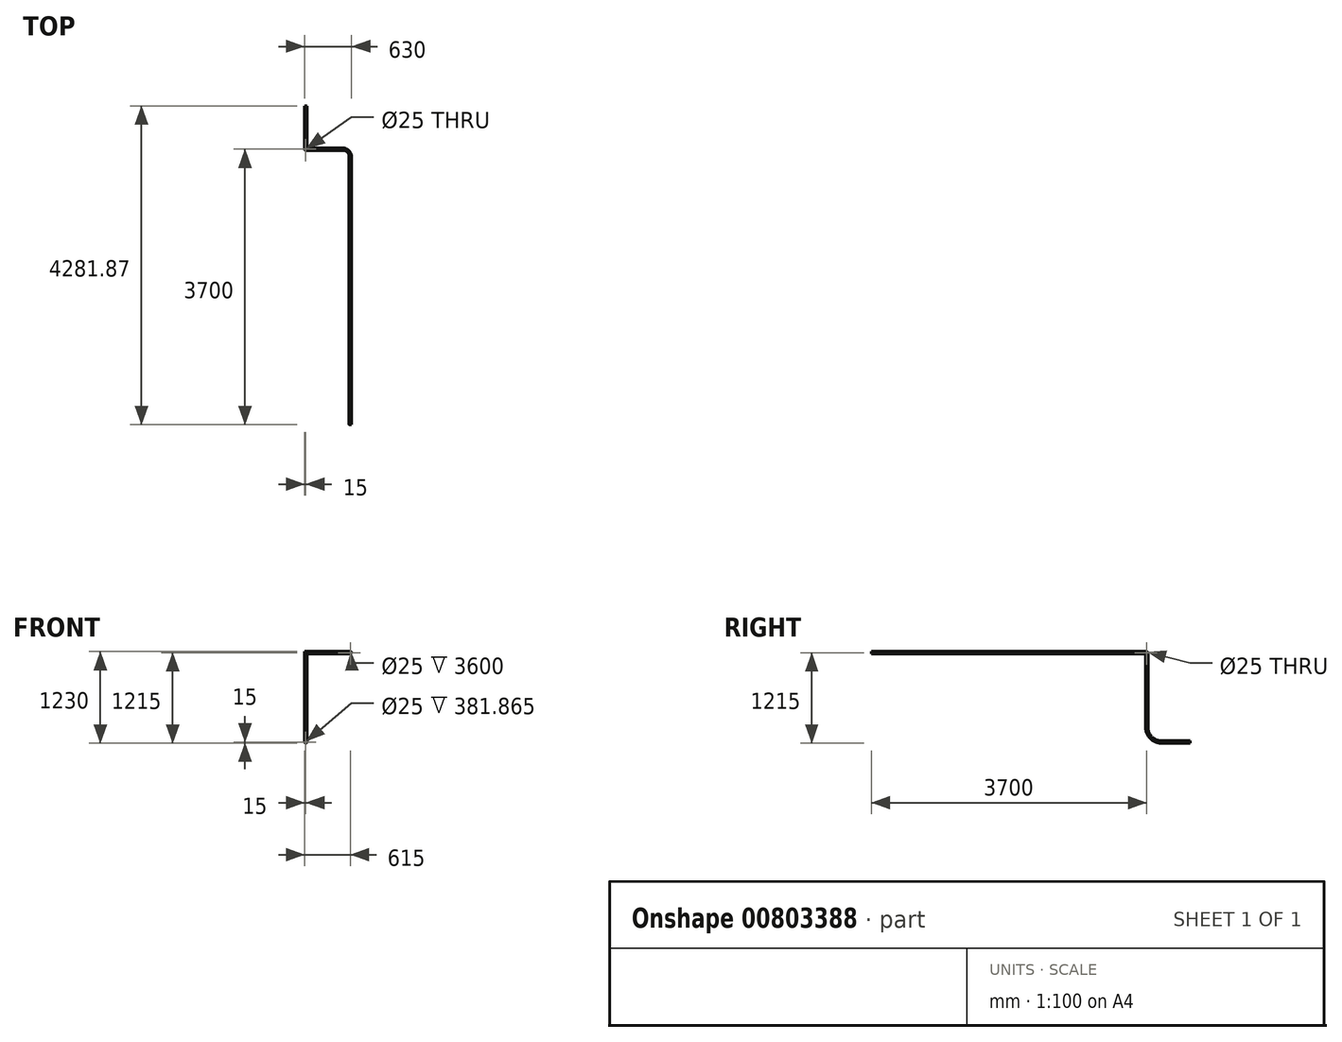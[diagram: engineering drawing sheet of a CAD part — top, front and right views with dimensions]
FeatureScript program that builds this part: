
annotation { "Feature Type Name" : "Feature", "Feature Type Description" : "" }
export const myFeature = defineFeature(function(context is Context, id is Id, definition is map)
    precondition{}
    {
        {
            var Q0;
            Q0=qCreatedBy(makeId("Front.planeOp"),FACE);
            var sketch = newSketch(context, id + "F0", { "sketchPlane" : qUnion([Q0])});
            skCircle(sketch, "E0", {"center": v(0, 0) * mm, "radius": 15 * mm});
            skCircle(sketch, "E1", {"center": v(0, 0) * mm, "radius": 12.5 * mm});
            skSolve(sketch);
        }
        {
            var Q0;
            Q0=qCreatedBy(makeId("Top.planeOp"),FACE);
            var sketch = newSketch(context, id + "F1", { "sketchPlane" : qUnion([Q0])});
            skLineSegment(sketch, "E2", {"start": v(0, 0) * mm, "end": v(0, 3600) * mm});
            skLineSegment(sketch, "E3", {"start": v(-100, 3700) * mm, "end": v(-600, 3700) * mm});
            skPoint(sketch, "E4.visualSharp", {"position": v(0, 3700) * mm});
            skArc(sketch, "E4.filletArc", {"start": v(0, 3600) * mm, "mid": v(-29.29, 3670.71) * mm, "end": v(-100, 3700) * mm});
            skSolve(sketch);
        }
        {
            var Q0;
            Q0=qCreatedBy(makeId("Right.planeOp"),FACE);
            cPlane(context, id + "F2", {"entities" : qUnion([Q0]), "cplaneType" : CPlaneType.OFFSET, "offset" : 600 * mm, "oppositeDirection" : true, "width" : 150 * mm, "height" : 150 * mm});
        }
        {
            var Q0;
            Q0=qCreatedBy(id+"F2.planeOp",FACE);
            var sketch = newSketch(context, id + "F3", { "sketchPlane" : qUnion([Q0])});
            skPoint(sketch, "E5.0", {"position": v(3700, 0) * mm});
            skLineSegment(sketch, "E6", {"start": v(3700, 0) * mm, "end": v(3700, -1000) * mm});
            skLineSegment(sketch, "E7", {"start": v(3900, -1200) * mm, "end": v(4281.87, -1200) * mm});
            skPoint(sketch, "E8.visualSharp", {"position": v(3700, -1200) * mm});
            skArc(sketch, "E8.filletArc", {"start": v(3700, -1000) * mm, "mid": v(3758.58, -1141.42) * mm, "end": v(3900, -1200) * mm});
            skSolve(sketch);
        }
        {
            var Q0;
            Q0=makeQuery(id+"F0.imprint","IMPRINT",FACE,{"disambiguationData":[TD([[makeQuery(id+"F0.imprint","IMPRINT",EDGE,{"derivedFrom":sQuery(id+"F0.wireOp",EDGE,"E0")}),1.0]])]});
            var Q1;
            Q1=sQuery(id+"F1.wireOp",EDGE,"E2");
            var Q2;
            Q2=sQuery(id+"F1.wireOp",EDGE,"E4.filletArc");
            var Q3;
            Q3=sQuery(id+"F1.wireOp",EDGE,"E3");
            var Q4;
            Q4=sQuery(id+"F3.wireOp",EDGE,"E6");
            var Q5;
            Q5=sQuery(id+"F3.wireOp",EDGE,"E8.filletArc");
            var Q6;
            Q6=sQuery(id+"F3.wireOp",EDGE,"E7");
            sweep(context, id + "F4", {"profiles" : qUnion([Q0]), "path" : qUnion([Q1, Q2, Q3, Q4, Q5, Q6])});
        }
    });
